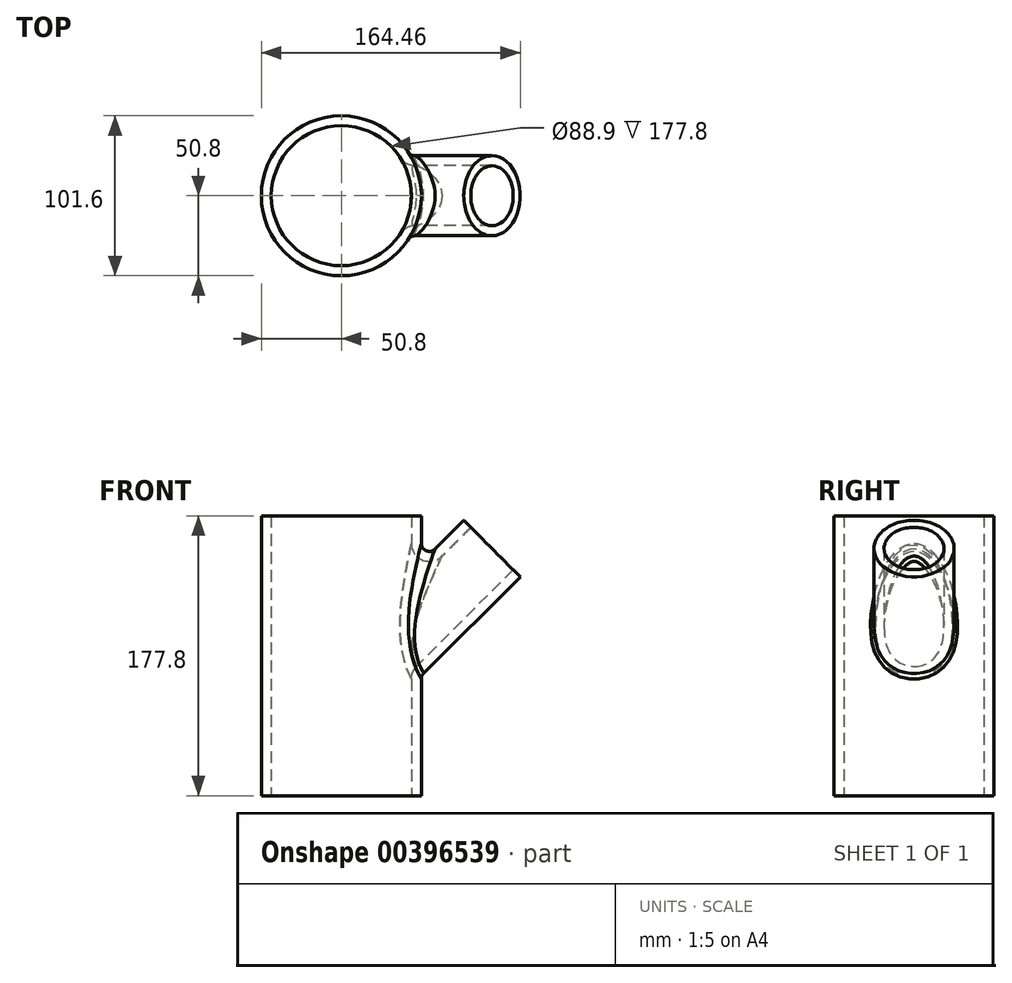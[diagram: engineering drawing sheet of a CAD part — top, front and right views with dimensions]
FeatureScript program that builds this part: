
annotation { "Feature Type Name" : "Feature", "Feature Type Description" : "" }
export const myFeature = defineFeature(function(context is Context, id is Id, definition is map)
    precondition{}
    {
        {
            var Q0;
            Q0=qCreatedBy(makeId("Front.planeOp"),FACE);
            var sketch = newSketch(context, id + "F0", { "sketchPlane" : qUnion([Q0])});
            skLineSegment(sketch, "E0", {"start": v(0, 0) * mm, "end": v(0, 177.8) * mm});
            skLineSegment(sketch, "E1", {"start": v(0, 177.8) * mm, "end": v(50.8, 177.8) * mm});
            skLineSegment(sketch, "E2", {"start": v(50.8, 177.8) * mm, "end": v(50.8, 0) * mm});
            skLineSegment(sketch, "E3", {"start": v(50.8, 0) * mm, "end": v(0, 0) * mm});
            skSolve(sketch);
        }
        {
            var Q0;
            Q0=qSketchRegion(id+"F0",true);
            var Q1;
            Q1=sQuery(id+"F0.wireOp",EDGE,"E0");
            revolve(context, id + "F1", {"entities" : qUnion([Q0]), "axis" : qUnion([Q1]), "revolveType" : RevolveType.FULL});
        }
        {
            var Q0;
            Q0=qCreatedBy(makeId("Front.planeOp"),FACE);
            var sketch = newSketch(context, id + "F2", { "sketchPlane" : qUnion([Q0])});
            skLineSegment(sketch, "E4", {"start": v(0, 61.32) * mm, "end": v(95.7, 157.02) * mm});
            skLineSegment(sketch, "E5", {"start": v(95.7, 157.02) * mm, "end": v(113.66, 139.06) * mm});
            skLineSegment(sketch, "E6", {"start": v(113.66, 139.06) * mm, "end": v(0, 25.4) * mm});
            skLineSegment(sketch, "E7", {"start": v(0, 25.4) * mm, "end": v(0, 61.32) * mm});
            skPoint(sketch, "E8", {"position": v(50.8, 76.2) * mm});
            skSolve(sketch);
        }
        {
            var Q0;
            Q0=qSketchRegion(id+"F2",true);
            var Q1;
            Q1=sQuery(id+"F2.wireOp",EDGE,"E4");
            revolve(context, id + "F3", {"operationType" : NewBodyOperationType.ADD, "entities" : qUnion([Q0]), "axis" : qUnion([Q1]), "revolveType" : RevolveType.FULL});
        }
        {
            var Q0;
            Q0=makeQuery(id+"F3.boolean.opBoolean","INTERSECT",EDGE,{"derivedFrom":[makeQuery(id+"F1.opRevolve","SWEPT_FACE",FACE,{"disambiguationData":[OSD([sQuery(id+"F0.wireOp",EDGE,"E2")])]}),makeQuery(id+"F3.opRevolve","SWEPT_FACE",FACE,{"disambiguationData":[OSD([sQuery(id+"F2.wireOp",EDGE,"E6")])]})]});
            fillet(context, id + "F4", {"entities" : qUnion([Q0]), "radius" : 5.08 * mm, "tangentPropagation" : true, "allowEdgeOverflow" : false});
        }
        {
            var Q0;
            Q0=makeQuery(id+"F1.opRevolve","SWEPT_FACE",FACE,{"disambiguationData":[OSD([sQuery(id+"F0.wireOp",EDGE,"E1")])]});
            var Q1;
            Q1=makeQuery(id+"F3.opRevolve","SWEPT_FACE",FACE,{"disambiguationData":[OSD([sQuery(id+"F2.wireOp",EDGE,"E5")])]});
            var Q2;
            Q2=makeQuery(id+"F1.opRevolve","SWEPT_FACE",FACE,{"disambiguationData":[OSD([sQuery(id+"F0.wireOp",EDGE,"E3")])]});
            shell(context, id + "F5", {"entities" : qUnion([Q0, Q1, Q2]), "thickness" : 6.35 * mm});
        }
    });
